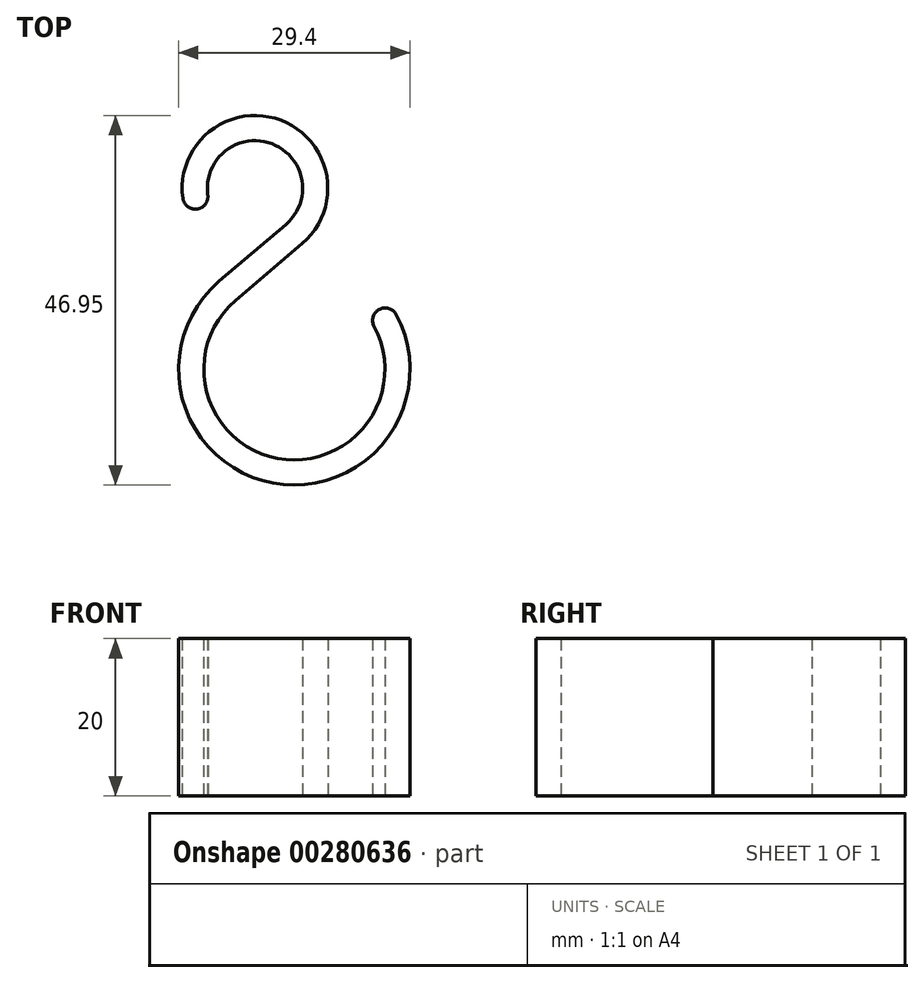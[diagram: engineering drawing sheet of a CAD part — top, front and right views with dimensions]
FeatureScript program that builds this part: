
annotation { "Feature Type Name" : "Feature", "Feature Type Description" : "" }
export const myFeature = defineFeature(function(context is Context, id is Id, definition is map)
    precondition{}
    {
        {
            var Q0;
            Q0=qCreatedBy(makeId("Top.planeOp"),FACE);
            var sketch = newSketch(context, id + "F0", { "sketchPlane" : qUnion([Q0])});
            skCircle(sketch, "E0", {"center": v(0, 0) * mm, "radius": 6.05 * mm});
            skCircle(sketch, "E1", {"center": v(5, -23) * mm, "radius": 11.5 * mm});
            skCircle(sketch, "E2", {"center": v(0, 0) * mm, "radius": 9.25 * mm});
            skCircle(sketch, "E3", {"center": v(5, -23) * mm, "radius": 14.7 * mm});
            skLineSegment(sketch, "E4", {"start": v(3.92, -4.6) * mm, "end": v(-4.53, -11.81) * mm});
            skLineSegment(sketch, "E5", {"start": v(6, -7.04) * mm, "end": v(-2.46, -14.25) * mm});
            skLineSegment(sketch, "E6", {"start": v(5, -23) * mm, "end": v(17, -14.5) * mm});
            skLineSegment(sketch, "E7", {"start": v(0, 0) * mm, "end": v(-8.7, -3.16) * mm});
            skSolve(sketch);
        }
        {
            var Q0;
            {var subQ4=sQuery(id+"F0.wireOp",EDGE,"E4");var subQ5=sQuery(id+"F0.wireOp",EDGE,"E0");var subQ6=makeQuery(id+"F0.imprint","INTERSECT",VERTEX,{"derivedFrom":[subQ5,subQ4]});Q0=makeQuery(id+"F0.imprint","IMPRINT",FACE,{"disambiguationData":[TD([[makeQuery(id+"F0.imprint","IMPRINT",EDGE,{"disambiguationData":[TD([[subQ6,-1.0]])],"derivedFrom":subQ5}),-1.0]])]});}
            var Q1;
            {var subQ4=sQuery(id+"F0.wireOp",EDGE,"E5");var subQ7=sQuery(id+"F0.wireOp",EDGE,"E1");var subQ8=makeQuery(id+"F0.imprint","INTERSECT",VERTEX,{"derivedFrom":[subQ7,subQ4]});Q1=makeQuery(id+"F0.imprint","IMPRINT",FACE,{"disambiguationData":[TD([[makeQuery(id+"F0.imprint","IMPRINT",EDGE,{"disambiguationData":[TD([[subQ8,-1.0]])],"derivedFrom":subQ7}),-1.0]])]});}
            var Q2;
            {var subQ0=sQuery(id+"F0.wireOp",EDGE,"E4");var subQ1=sQuery(id+"F0.wireOp",EDGE,"E2");var subQ2=makeQuery(id+"F0.imprint","INTERSECT",VERTEX,{"derivedFrom":[subQ1,subQ0]});Q2=makeQuery(id+"F0.imprint","IMPRINT",FACE,{"disambiguationData":[TD([[makeQuery(id+"F0.imprint","IMPRINT",EDGE,{"disambiguationData":[TD([[subQ2,-1.0]])],"derivedFrom":subQ1}),-1.0]])]});}
            var Q3;
            {var subQ0=sQuery(id+"F0.wireOp",EDGE,"E3");var subQ1=sQuery(id+"F0.wireOp",EDGE,"E2");var subQ2=makeQuery(id+"F0.imprint","INTERSECT",VERTEX,{"disambiguationData":[OD(0.0)],"derivedFrom":[subQ1,subQ0]});Q3=makeQuery(id+"F0.imprint","IMPRINT",FACE,{"disambiguationData":[TD([[makeQuery(id+"F0.imprint","IMPRINT",EDGE,{"disambiguationData":[TD([[subQ2,-1.0]])],"derivedFrom":subQ1}),1.0]])]});}
            var Q4;
            {var subQ0=sQuery(id+"F0.wireOp",EDGE,"E5");var subQ1=sQuery(id+"F0.wireOp",EDGE,"E2");var subQ2=makeQuery(id+"F0.imprint","INTERSECT",VERTEX,{"derivedFrom":[subQ1,subQ0]});Q4=makeQuery(id+"F0.imprint","IMPRINT",FACE,{"disambiguationData":[TD([[makeQuery(id+"F0.imprint","IMPRINT",EDGE,{"disambiguationData":[TD([[subQ2,1.0]])],"derivedFrom":subQ1}),-1.0]])]});}
            extrude(context, id + "F1", {"entities" : qUnion([Q0, Q1, Q2, Q3, Q4]), "depth" : 20 * mm});
        }
        {
            var Q0;
            Q0=makeQuery(id+"F1.opExtrude","SWEPT_EDGE",EDGE,{"disambiguationData":[OSD([sQuery(id+"F0.wireOp",EDGE,"E3"),sQuery(id+"F0.wireOp",EDGE,"E6")])]});
            var Q1;
            Q1=makeQuery(id+"F1.opExtrude","SWEPT_EDGE",EDGE,{"disambiguationData":[OSD([sQuery(id+"F0.wireOp",EDGE,"E1"),sQuery(id+"F0.wireOp",EDGE,"E6")])]});
            var Q2;
            Q2=makeQuery(id+"F1.opExtrude","SWEPT_EDGE",EDGE,{"disambiguationData":[OSD([sQuery(id+"F0.wireOp",EDGE,"E2"),sQuery(id+"F0.wireOp",EDGE,"E7")])]});
            var Q3;
            Q3=makeQuery(id+"F1.opExtrude","SWEPT_EDGE",EDGE,{"disambiguationData":[OSD([sQuery(id+"F0.wireOp",EDGE,"E0"),sQuery(id+"F0.wireOp",EDGE,"E7")])]});
            fillet(context, id + "F2", {"entities" : qUnion([Q0, Q1, Q2, Q3]), "radius" : 1.6 * mm, "tangentPropagation" : true, "allowEdgeOverflow" : false});
        }
    });
